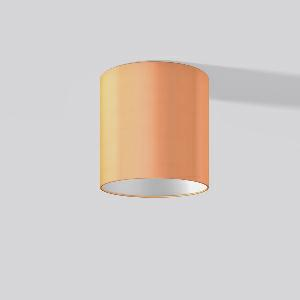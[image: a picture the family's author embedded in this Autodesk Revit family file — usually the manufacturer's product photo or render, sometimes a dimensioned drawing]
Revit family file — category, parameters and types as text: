
# Revit family: toledo_flatliner_901634_002_9799
name_source: partatom
category: Lighting Fixtures
units: mm (PartAtom-declared; Revit-internal decimal feet)

## family parameters
Cut with Voids When Loaded = No
Host = Face
Light Source = No
Part Type = Normal
Room Calculation Point = No
Round Connector Dimension = Use Diameter
Shared = No

## types (1)
- 982302.002 (1 x LED Modul 830, 1700 lm, 3000)
    Apparent Load = 22 VA
    CIE Flux Codes = 50 82 97 99 100
    Color Rendering = 80
    Color Temperature = 3000
    Default Elevation = 1800 mm
    Description = Series: TOLEDO FLATLINER
Decorative ceiling luminaire for interior decoration. Base luminaire prepared for the installation of fabric lampshade. Cylinder housing sheet steel, powder-coated. Housing: die cast aluminium and sheet steel, powder-coated. Bezel ring: die-cast aluminium, powder-coated. Lightguide and diffuser made of non-yellowing plastic (PMMA) opal matt. Modular design: With the basic luminaire, a square or cylindrical fabric lampshade must always be ordered separately. Fabric lampshades can be fitted to the basic luminaire without tools. Order satin finish diffuser as separate accessory. 
Colour: white
Diameter: 330 mm
Height: 70 mm
Lamp: LED
Socket: without socket
Colour temperature: 3000K
Colour rendering index (CRI): 80
System power: 22 W
Rated luminous flux: 1700 lm
Luminous efficiency: 77 lm/W
Control gear: Regulated power supply
Protection class: II
Type of protection: IP 40
    Height = 70 mm
    Lamp = 1 x LED Modul 830
    Lamp Light Flux = 1700 lm
    Lamp count = 1
    Length = 330 mm
    Lifetime = 50000 h
    Luminous efficacy = 77 lm/W
    Manufacturer = RZB
    ModVariant = No
    Model = 901634.002
    Mounting Place = Ceiling
    Mounting Type = Surface mounted
    Number of Poles = 1
    OnlyDefault = Yes
    Power Factor = 1
    Product Name = TOLEDO FLATLINER
    Product group = Surface mounted ceiling Fabric lampshade luminaires
    ProductGroupID = 313
    Protection Class = Protection class II
    Protection Degree = IP 40
    RLX_Detail_Level = 1
    RLX_Emergency_Light_Flux = 0 lm
    RLX_Emergency_Type = 0
    RLX_Emergency_Type_DB = No
    RlxData = <blob elided: 62797 chars, md5=ea8ac3b7>
    Socket = socket
    Standby Power = 0 W
    System Light Flux = 1700 lm
    System Power = 22 W
    Type Image = toledo_flatliner_anbau_rund_orange_odeckel.jpg
    URL = http://relux.com
    VarID = 982302_002_891e
    Voltage = 230 V
    Voltage Range = 220-240 V
    Weight = 0.00 kg
    Width = 0 mm  [stored 0 ft]

note: [stored X ft] marks values corroborated as IEEE doubles in the binary element streams (Revit-internal decimal feet)

## geometry (parser evidence)
native form markers: Blend x4, Sweep x8
no freeform markers — native parametric forms only
